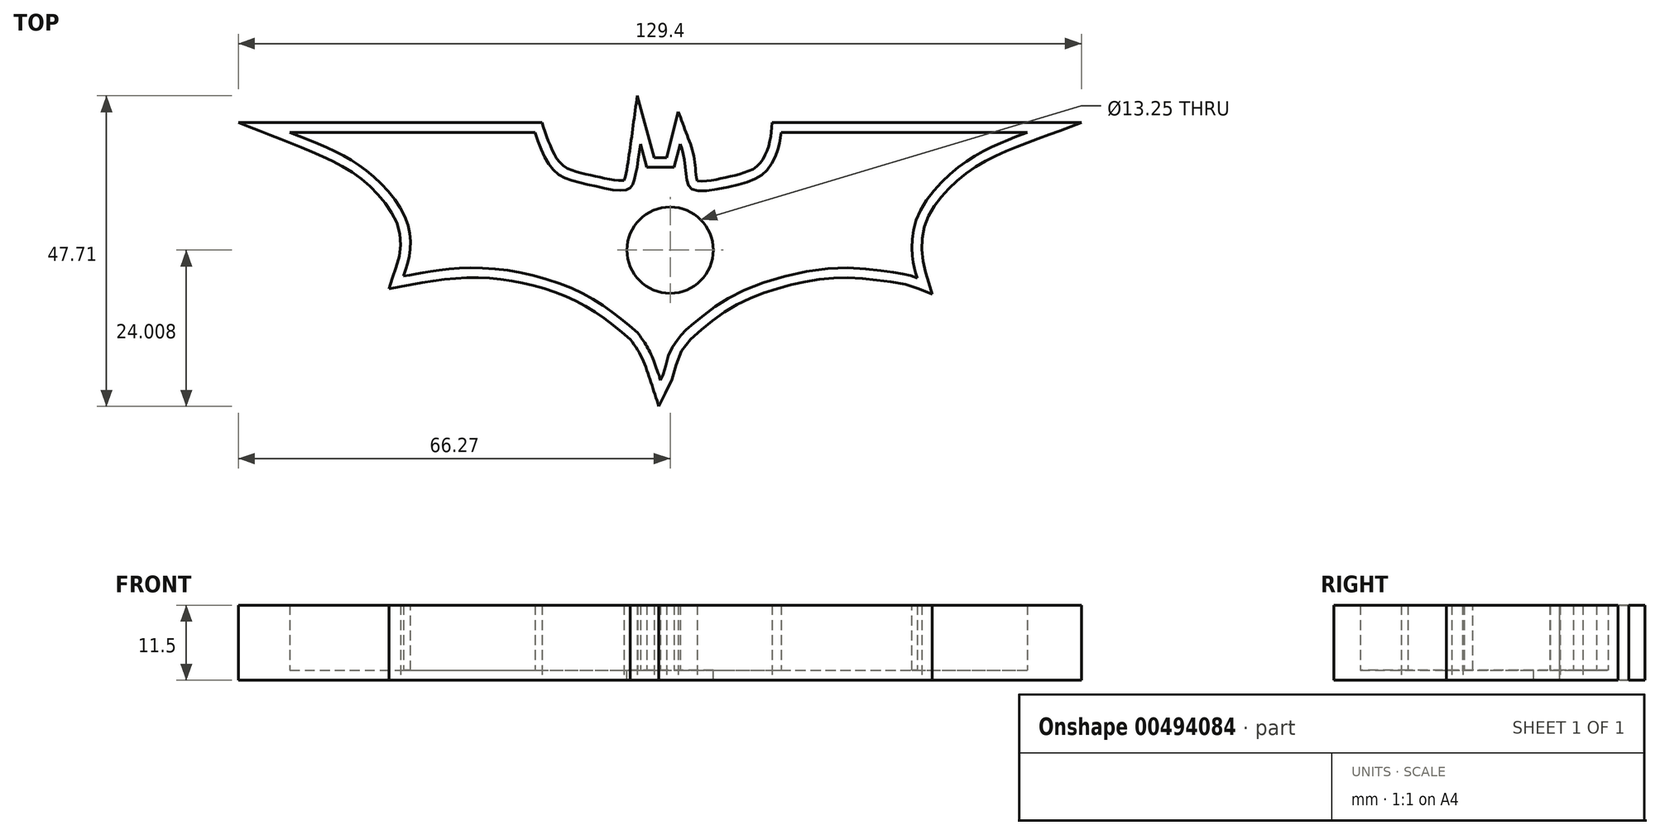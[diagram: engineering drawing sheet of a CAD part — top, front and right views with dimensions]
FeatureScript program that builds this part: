
annotation { "Feature Type Name" : "Feature", "Feature Type Description" : "" }
export const myFeature = defineFeature(function(context is Context, id is Id, definition is map)
    precondition{}
    {
        {
            var Q0;
            Q0=qCreatedBy(makeId("Top.planeOp"),FACE);
            var sketch = newSketch(context, id + "F0", { "sketchPlane" : qUnion([Q0])});
            skLineSegment(sketch, "E0", {"start": v(-58.36, 14.7) * mm, "end": v(-20.75, 14.7) * mm});
            skFitSpline(sketch, "E1", {"points": [v(-20.75, 14.7) * mm, v(-17.63, 8.65) * mm, v(-12.22, 6.62) * mm, v(-6.59, 5.92) * mm, v(-5.44, 7.6) * mm, v(-4.55, 12.92) * mm], "startDerivative": vector(10.58, -30.28) * mm, "endDerivative": vector(3.9, 28.44) * mm});
            skFitSpline(sketch, "E2", {"points": [v(-4.55, 12.92) * mm, v(-3.56, 9.35) * mm], "startDerivative": vector(0.99, -3.56) * mm, "endDerivative": vector(0.99, -3.56) * mm});
            skFitSpline(sketch, "E3", {"points": [v(-3.56, 9.35) * mm, v(0.6, 9.35) * mm], "startDerivative": vector(4.17, 0) * mm, "endDerivative": vector(4.17, 0) * mm});
            skFitSpline(sketch, "E4", {"points": [v(0.6, 9.35) * mm, v(1.53, 12.92) * mm], "startDerivative": vector(0.92, 3.56) * mm, "endDerivative": vector(0.92, 3.56) * mm});
            skFitSpline(sketch, "E5", {"points": [v(1.53, 12.92) * mm, v(2.13, 10.94) * mm, v(2.54, 7.6) * mm, v(3.47, 5.92) * mm, v(10.08, 6.62) * mm, v(14.64, 8.65) * mm, v(16.6, 12.34) * mm, v(17.02, 14.7) * mm], "startDerivative": vector(6.16, -16.24) * mm, "endDerivative": vector(2.02, 18.43) * mm});
            skLineSegment(sketch, "E6", {"start": v(17.02, 14.7) * mm, "end": v(54.81, 14.7) * mm});
            skFitSpline(sketch, "E7", {"points": [v(-58.36, 14.7) * mm, v(-51.28, 11.7) * mm, v(-45.6, 8.02) * mm, v(-40.66, 1.63) * mm, v(-39.94, -3.59) * mm, v(-40.93, -7.37) * mm], "startDerivative": vector(33.12, -13.03) * mm, "endDerivative": vector(-7.78, -22.9) * mm});
            skFitSpline(sketch, "E8", {"points": [v(-40.93, -7.37) * mm, v(-37.1, -6.7) * mm, v(-27.75, -6.16) * mm, v(-13.85, -9.8) * mm, v(-5, -16.03) * mm], "startDerivative": vector(21.19, 4.03) * mm, "endDerivative": vector(29.37, -24.84) * mm});
            skFitSpline(sketch, "E9", {"points": [v(-5, -16.03) * mm, v(-3.18, -18.87) * mm, v(-1.46, -23.36) * mm], "startDerivative": vector(4.19, -5.76) * mm, "endDerivative": vector(2.91, -8.8) * mm});
            skFitSpline(sketch, "E10", {"points": [v(-1.46, -23.36) * mm, v(-0.82, -21.77) * mm, v(0, -18.87) * mm, v(1.32, -16.9) * mm, v(2.01, -16.03) * mm, v(4.58, -13.79) * mm, v(10.79, -9.8) * mm, v(24.7, -6.16) * mm, v(33.55, -6.7) * mm, v(36.43, -7.15) * mm, v(37.9, -7.63) * mm], "startDerivative": vector(10.47, 21.85) * mm, "endDerivative": vector(22.32, -8.3) * mm});
            skFitSpline(sketch, "E11", {"points": [v(37.9, -7.63) * mm, v(37.5, -6.16) * mm, v(37.14, -3.59) * mm, v(37.9, 1.63) * mm, v(42.63, 8.02) * mm, v(47.84, 11.7) * mm, v(52.3, 13.74) * mm, v(54.81, 14.7) * mm], "startDerivative": vector(-5.05, 16.16) * mm, "endDerivative": vector(20.46, 7.62) * mm});
            skSolve(sketch);
        }
        {
            var Q0;
            Q0=makeQuery(id+"F0.imprint","IMPRINT",FACE,{"disambiguationData":[TD([[makeQuery(id+"F0.imprint","IMPRINT",EDGE,{"derivedFrom":sQuery(id+"F0.wireOp",EDGE,"E0")}),-1.0]])]});
            extrude(context, id + "F1", {"entities" : qUnion([Q0]), "depth" : 10 * mm});
        }
        {
            var Q0;
            Q0=makeQuery(id+"F1.opExtrude","CAP_FACE",FACE,{"disambiguationData":[OSD([sQuery(id+"F0.wireOp",EDGE,"E0"),sQuery(id+"F0.wireOp",EDGE,"E1"),sQuery(id+"F0.wireOp",EDGE,"E2"),sQuery(id+"F0.wireOp",EDGE,"E3"),sQuery(id+"F0.wireOp",EDGE,"E4"),sQuery(id+"F0.wireOp",EDGE,"E5"),sQuery(id+"F0.wireOp",EDGE,"E6"),sQuery(id+"F0.wireOp",EDGE,"E7"),sQuery(id+"F0.wireOp",EDGE,"E8"),sQuery(id+"F0.wireOp",EDGE,"E9"),sQuery(id+"F0.wireOp",EDGE,"E10"),sQuery(id+"F0.wireOp",EDGE,"E11")])],"isStart":false});
            shell(context, id + "F2", {"entities" : qUnion([Q0]), "thickness" : 1.5 * mm, "oppositeDirection" : true});
        }
        {
            var Q0;
            Q0=makeQuery(id+"F2.opShell","OFFSET_FACE",FACE,{"disambiguationData":[OSD([sQuery(id+"F0.wireOp",EDGE,"E0"),sQuery(id+"F0.wireOp",EDGE,"E1"),sQuery(id+"F0.wireOp",EDGE,"E2"),sQuery(id+"F0.wireOp",EDGE,"E3"),sQuery(id+"F0.wireOp",EDGE,"E4"),sQuery(id+"F0.wireOp",EDGE,"E5"),sQuery(id+"F0.wireOp",EDGE,"E6"),sQuery(id+"F0.wireOp",EDGE,"E7"),sQuery(id+"F0.wireOp",EDGE,"E8"),sQuery(id+"F0.wireOp",EDGE,"E9"),sQuery(id+"F0.wireOp",EDGE,"E10"),sQuery(id+"F0.wireOp",EDGE,"E11")])]});
            var sketch = newSketch(context, id + "F3", { "sketchPlane" : qUnion([Q0])});
            skCircle(sketch, "E12", {"center": v(0, -3.36) * mm, "radius": 6.62 * mm});
            skSolve(sketch);
        }
        {
            var Q0;
            Q0 = qSketchRegion(id + "F3", true);
            extrude(context, id + "F4", {"entities" : qUnion([Q0]), "operationType" : NewBodyOperationType.REMOVE, "oppositeDirection" : true, "depth" : 25 * mm});
        }
    });
